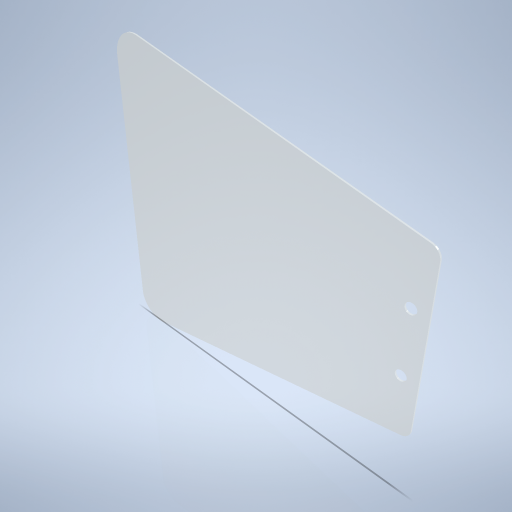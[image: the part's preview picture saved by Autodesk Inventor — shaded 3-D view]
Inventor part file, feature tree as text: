
AUTODESK INVENTOR PART (.ipt)
format: ipt  version: 2024.2 (Build 282272000, 272)  size: 265,216 bytes
history: native  units: mm
features: other x2, fillet x2, sketch x2, hole x1
ambient origin geometry x8: Origin, YZ Plane, XZ Plane, XY Plane, X Axis, Y Axis, Z Axis, Center Point
bodies: Volumenkörper1 (feature_tree)
feature tree (7):
  other  "Fläche1"
  hole  "Bohrung2"  [1 undecoded]
  fillet  "Rundung1"  Radius=50.0mm
  fillet  "Rundung2"  Radius=0.5mm
  sketch  "Skizze1"  dims[d0=90.0mm d1=95.0mm d2=50.0mm d3=0.5mm]
  other  "Grobblech1"
  sketch  "Skizze3"  dims[d16=16.0mm d17=16.0mm d18=4.5mm d19=4.5mm d20=3.0mm d21=6.0mm d22=4.0mm d23=2.0mm d24=90.0deg d25=8.0mm d26=20.594885mm d27=7.0mm d28=3.0mm]
note: 1 required parameter value undecoded (feature->parameter linkage not recoverable at this tier; creation-order binding heuristic only, values carry confidence <= 0.55)
